FCSTD DOCUMENT  (FreeCAD 1.1R39747 (Git))
Label: variables
License: All rights reserved
LicenseURL: https://en.wikipedia.org/wiki/All_rights_reserved
objects: Spreadsheet::Sheet×1

FEATURE [Spreadsheet::Sheet] Spreadsheet  label="variables"
  MountType = 0
  ServoType = 0
  cells = A2='Pincher Length (35mm Minimum); B2='Tollerance; C2='Claw Back Spacer Diameter; D2='Claw Back Outer Spacer Holes Wing Angle; E2='Claw Pincher C2C; F2='Claw Base Thickness; G2='Claw Back Spacer Length; H2='3DP Shaft Diam; I2='Claw Spacer Screw Length; J2='Camera Mount Pillar Len; K2='Camera Mount Pillar Thickness; L2='Distance Bearing Holes to End; M2='Claw Short Wall Distance; N2='Camera Mount; O2='Hub Mount Countersink; A3(claw_pincher_length)=35; B3(tollerance)=0.3; C3(claw_back_spacer_diameter)=8; D3(claw_back_outer_spacer_holes_wing_angle)=150; E3(claw_pincher_c2c)=35; F3(claw_base_thickness)=8.7; G3(claw_back_spacer_length)=22; H3(shaft_diam)=7.8; I3(claw_spacer_screw_len)=45; J3(camera_mount_pillar_len)=16; K3(camera_mount_pillar_thickness)=7; L3(distance_bearing_holes_to_end)=16; M3(claw_short_wall_distance)=30; N3(use_camera_mount)=0; O3(Hub_Mount_Countersink)=1; A5='Servo; B5='HolesToSpline; C5='HolesHorizDistance; D5='HolesVertDistance; E5='GobildaSrvVisible; F5='DSServoVisible; A6==hiddenref(.ServoType.String); B6(servo_holes_to_spline)==.B7; C6(servo_holes_horiz_dist)==.C7; D6(servo_holes_vert_dist)==.D7; E6(gobilda_servo_visible)==.E7; F6(dsservo_visible)==.F7; A7='DSServo; B7=14.75; C7=49.5; D7=9.9; E7=0; F7=1; A8='Gobilda; B8=14.2; C8=48; D8=9.9; E8=1; F8=0; A11='Mount Type; B11='Rex Mount; C11='Hub Mount; A12==hiddenref(.MountType.String); B12(rex_mount)==.B13; C12(hub_mount)==.C13; A13='Rex Mount; B13=1; C13=0; A14='Hub Mount; B14=0; C14=1
  expr: .MountType.Enum = cells[<<A13:|>>]
  expr: .ServoType.Enum = cells[<<A7:|>>]
  expr: .cells.Bind.B12.C12 = tuple(.cells; <<B>> + str(hiddenref(MountType) + 13); <<C>> + str(hiddenref(MountType) + 13))
  expr: .cells.Bind.B6.F6 = tuple(.cells; <<B>> + str(hiddenref(ServoType) + 7); <<F>> + str(hiddenref(ServoType) + 7))
